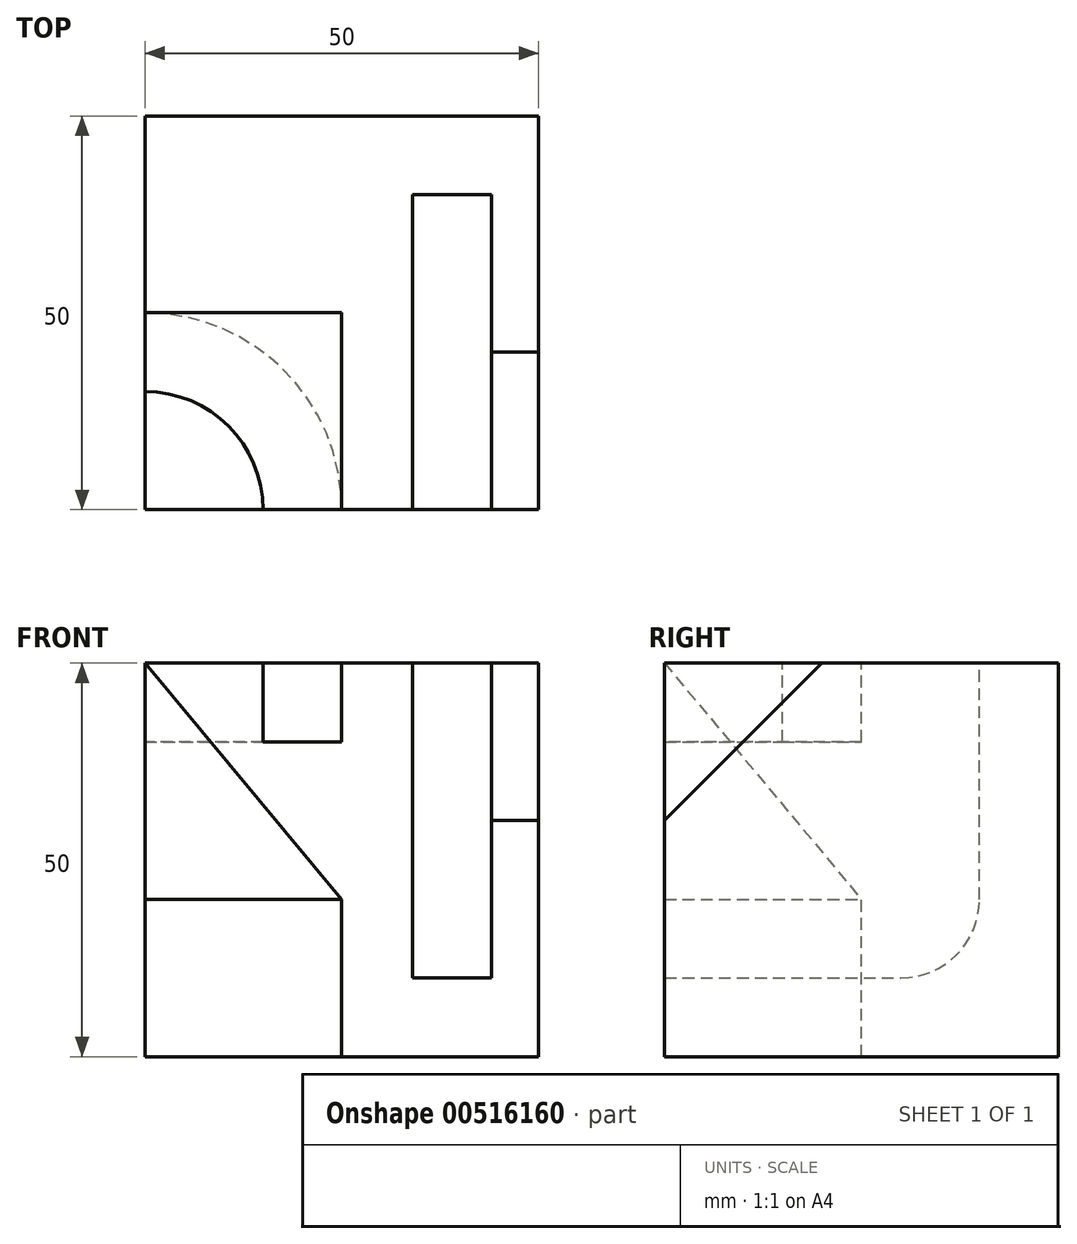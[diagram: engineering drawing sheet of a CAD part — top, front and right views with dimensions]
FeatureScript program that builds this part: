
annotation { "Feature Type Name" : "Feature", "Feature Type Description" : "" }
export const myFeature = defineFeature(function(context is Context, id is Id, definition is map)
    precondition{}
    {
        {
            var Q0;
            Q0=qCreatedBy(makeId("Top.planeOp"),FACE);
            var sketch = newSketch(context, id + "F0", { "sketchPlane" : qUnion([Q0])});
            skLineSegment(sketch, "E0.bottom", {"start": v(0, 0) * mm, "end": v(50, 0) * mm});
            skLineSegment(sketch, "E0.top", {"start": v(0, 50) * mm, "end": v(50, 50) * mm});
            skLineSegment(sketch, "E0.left", {"start": v(0, 0) * mm, "end": v(0, 50) * mm});
            skLineSegment(sketch, "E0.right", {"start": v(50, 0) * mm, "end": v(50, 50) * mm});
            skSolve(sketch);
        }
        {
            var Q0;
            Q0 = qSketchRegion(id + "F0", true);
            extrude(context, id + "F1", {"entities" : qUnion([Q0]), "depth" : 50 * mm, "offsetDistance" : 25 * mm});
        }
        {
            var Q0;
            Q0=makeQuery(id+"F1.opExtrude","SWEPT_FACE",FACE,{"disambiguationData":[OSD([sQuery(id+"F0.wireOp",EDGE,"E0.right")])]});
            var sketch = newSketch(context, id + "F2", { "sketchPlane" : qUnion([Q0])});
            skLineSegment(sketch, "E1", {"start": v(0, 30) * mm, "end": v(20, 50) * mm});
            skSolve(sketch);
        }
        {
            var Q0;
            Q0=makeQuery(id+"F1.opExtrude","SWEPT_FACE",FACE,{"disambiguationData":[OSD([sQuery(id+"F0.wireOp",EDGE,"E0.left")])]});
            cPlane(context, id + "F3", {"entities" : qUnion([Q0]), "cplaneType" : CPlaneType.OFFSET, "offset" : 34 * mm, "oppositeDirection" : true, "width" : 150 * mm, "height" : 150 * mm});
        }
        {
            var Q0;
            Q0=qCreatedBy(id+"F3.planeOp",FACE);
            cPlane(context, id + "F4", {"entities" : qUnion([Q0]), "cplaneType" : CPlaneType.OFFSET, "offset" : 10 * mm, "oppositeDirection" : true, "width" : 150 * mm, "height" : 150 * mm});
        }
        {
            var Q0;
            {var subQ0=sQuery(id+"F2.wireOp",EDGE,"E1");Q0=makeQuery(id+"F2.imprint","IMPRINT",FACE,{"disambiguationData":[TD([[makeQuery(id+"F2.imprint","IMPRINT",EDGE,{"derivedFrom":subQ0}),1.0]])]});}
            var Q1;
            Q1=qCreatedBy(id+"F4.planeOp",FACE);
            extrude(context, id + "F5", {"entities" : qUnion([Q0]), "operationType" : NewBodyOperationType.REMOVE, "endBound" : BoundingType.UP_TO_SURFACE, "oppositeDirection" : true, "depth" : 25 * mm, "endBoundEntityFace" : qUnion([Q1]), "offsetDistance" : 25 * mm});
        }
        {
            var Q0;
            Q0=makeQuery(id+"F1.opExtrude","CAP_FACE",FACE,{"disambiguationData":[OSD([sQuery(id+"F0.wireOp",EDGE,"E0.bottom"),sQuery(id+"F0.wireOp",EDGE,"E0.top"),sQuery(id+"F0.wireOp",EDGE,"E0.left"),sQuery(id+"F0.wireOp",EDGE,"E0.right")])],"isStart":false});
            var sketch = newSketch(context, id + "F6", { "sketchPlane" : qUnion([Q0])});
            skLineSegment(sketch, "E2.bottom", {"start": v(44, 0) * mm, "end": v(34, 0) * mm});
            skLineSegment(sketch, "E2.top", {"start": v(44, 40) * mm, "end": v(34, 40) * mm});
            skLineSegment(sketch, "E2.left", {"start": v(44, 0) * mm, "end": v(44, 40) * mm});
            skLineSegment(sketch, "E2.right", {"start": v(34, 0) * mm, "end": v(34, 40) * mm});
            skSolve(sketch);
        }
        {
            var Q0;
            Q0=makeQuery(id+"F1.opExtrude","CAP_FACE",FACE,{"disambiguationData":[OSD([sQuery(id+"F0.wireOp",EDGE,"E0.bottom"),sQuery(id+"F0.wireOp",EDGE,"E0.top"),sQuery(id+"F0.wireOp",EDGE,"E0.left"),sQuery(id+"F0.wireOp",EDGE,"E0.right")])],"isStart":true});
            cPlane(context, id + "F7", {"entities" : qUnion([Q0]), "cplaneType" : CPlaneType.OFFSET, "offset" : 10 * mm, "oppositeDirection" : true, "width" : 150 * mm, "height" : 150 * mm});
        }
        {
            var Q0;
            {var subQ3=sQuery(id+"F6.wireOp",EDGE,"E2.bottom");Q0=makeQuery(id+"F6.imprint","IMPRINT",FACE,{"disambiguationData":[TD([[makeQuery(id+"F6.imprint","IMPRINT",EDGE,{"derivedFrom":subQ3}),1.0]])]});}
            var Q1;
            Q1=qCreatedBy(id+"F7.planeOp",FACE);
            extrude(context, id + "F8", {"entities" : qUnion([Q0]), "operationType" : NewBodyOperationType.REMOVE, "endBound" : BoundingType.UP_TO_SURFACE, "oppositeDirection" : true, "depth" : 25 * mm, "endBoundEntityFace" : qUnion([Q1]), "offsetDistance" : 25 * mm});
        }
        {
            var Q0;
            Q0=makeQuery(id+"F8.boolean.opBoolean","COPY",EDGE,{"derivedFrom":makeQuery(id+"F8.opExtrude","CAP_EDGE",EDGE,{"disambiguationData":[OSD([sQuery(id+"F6.wireOp",EDGE,"E2.top")])],"isStart":false})});
            fillet(context, id + "F9", {"entities" : qUnion([Q0]), "radius" : 10 * mm, "tangentPropagation" : true, "allowEdgeOverflow" : false});
        }
        {
            var Q0;
            Q0=makeQuery(id+"F1.opExtrude","CAP_FACE",FACE,{"disambiguationData":[OSD([sQuery(id+"F0.wireOp",EDGE,"E0.bottom"),sQuery(id+"F0.wireOp",EDGE,"E0.top"),sQuery(id+"F0.wireOp",EDGE,"E0.left"),sQuery(id+"F0.wireOp",EDGE,"E0.right")])],"isStart":false});
            var sketch = newSketch(context, id + "F10", { "sketchPlane" : qUnion([Q0])});
            skCircle(sketch, "E3", {"center": v(0, 0) * mm, "radius": 15 * mm});
            skCircle(sketch, "E4", {"center": v(0, -20.5) * mm, "radius": 1 * mm});
            skSolve(sketch);
        }
        {
            var Q0;
            Q0=makeQuery(id+"F1.opExtrude","SWEPT_FACE",FACE,{"disambiguationData":[OSD([sQuery(id+"F0.wireOp",EDGE,"E0.bottom")])]});
            var sketch = newSketch(context, id + "F11", { "sketchPlane" : qUnion([Q0])});
            skLineSegment(sketch, "E5", {"start": v(0, 50) * mm, "end": v(25, 20) * mm});
            skLineSegment(sketch, "E6", {"start": v(25, 20) * mm, "end": v(0, 20) * mm});
            skLineSegment(sketch, "E7", {"start": v(0, 20) * mm, "end": v(0, 50) * mm});
            skSolve(sketch);
        }
        {
            var Q0;
            Q0=makeQuery(id+"F11.imprint","IMPRINT",FACE,{"disambiguationData":[TD([[makeQuery(id+"F11.imprint","IMPRINT",EDGE,{"derivedFrom":sQuery(id+"F11.wireOp",EDGE,"E5")}),-1.0]])]});
            var Q1;
            Q1=sQuery(id+"F10.wireOp",EDGE,"E3");
            sweep(context, id + "F12", {"operationType" : NewBodyOperationType.REMOVE, "profiles" : qUnion([Q0]), "path" : qUnion([Q1])});
        }
        {
            var Q0;
            Q0=makeQuery(id+"F12.boolean.opBoolean","COPY",FACE,{"derivedFrom":makeQuery(id+"F12.opSweep","SWEPT_FACE",FACE,{"disambiguationData":[OSD([sQuery(id+"F10.wireOp",EDGE,"E3"),sQuery(id+"F11.wireOp",EDGE,"E6")])]})});
            extrude(context, id + "F13", {"entities" : qUnion([Q0]), "operationType" : NewBodyOperationType.REMOVE, "endBound" : BoundingType.THROUGH_ALL, "oppositeDirection" : true, "depth" : 25 * mm, "offsetDistance" : 25 * mm});
        }
        {
            var Q0;
            Q0=makeQuery(id+"F1.opExtrude","CAP_FACE",FACE,{"disambiguationData":[OSD([sQuery(id+"F0.wireOp",EDGE,"E0.bottom"),sQuery(id+"F0.wireOp",EDGE,"E0.top"),sQuery(id+"F0.wireOp",EDGE,"E0.left"),sQuery(id+"F0.wireOp",EDGE,"E0.right")])],"isStart":false});
            var sketch = newSketch(context, id + "F14", { "sketchPlane" : qUnion([Q0])});
            skLineSegment(sketch, "E8", {"start": v(0, 25) * mm, "end": v(25, 25) * mm});
            skLineSegment(sketch, "E9", {"start": v(25, 25) * mm, "end": v(25, 0) * mm});
            skCircle(sketch, "E10", {"center": v(0, 0) * mm, "radius": 15 * mm});
            skSolve(sketch);
        }
        {
            var Q0;
            {var subQ5=sQuery(id+"F14.wireOp",EDGE,"E8");Q0=makeQuery(id+"F14.imprint","IMPRINT",FACE,{"disambiguationData":[TD([[makeQuery(id+"F14.imprint","IMPRINT",EDGE,{"derivedFrom":subQ5}),-1.0]])]});}
            extrude(context, id + "F15", {"entities" : qUnion([Q0]), "operationType" : NewBodyOperationType.REMOVE, "oppositeDirection" : true, "depth" : 10 * mm, "offsetDistance" : 25 * mm});
        }
    });
